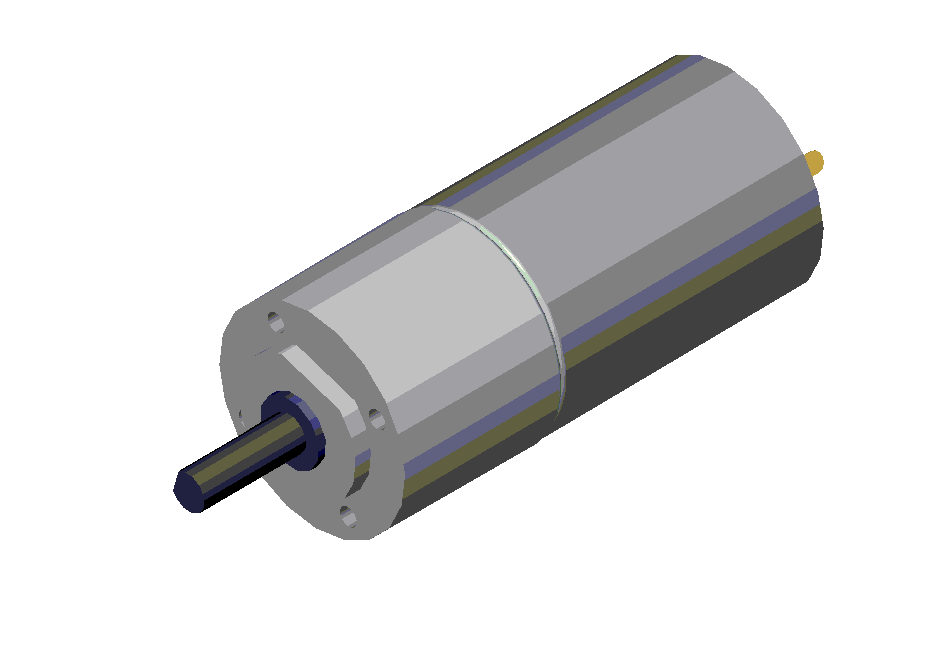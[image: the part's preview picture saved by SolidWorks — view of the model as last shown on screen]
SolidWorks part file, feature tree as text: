
SOLIDWORKS PART (.sldprt)
format: sldprt  version: not decoded by parser v0  size: 169,472 bytes
history: native  units: mm
features: sketch x9, extrude x7, fillet x5, cut_extrude x2, pattern_circular x1 (+8 scaffold rows collapsed)
feature tree (32):
  scaffold x8  (default folders/planes/origin — collapsed)
  sketch  "Sketch1"  dims[D1=21.9mm]
  extrude  "Base-Extrude"  Depth=18mm
  sketch  "Sketch3"  dims[D1=13.88mm D2=5.94mm D3=11.88mm]
  extrude  "Boss-Extrude1"  Depth=1.75mm
  sketch  "Sketch4"  dims[D1=7.01mm]
  extrude  "Boss-Extrude2"  Depth=0.8mm
  sketch  "Sketch5"  dims[D1=3.89mm]
  extrude  "Boss-Extrude3"  Depth=11.5mm
  fillet  "Fillet1"  Radius=0.5mm
  sketch  "Sketch6"  dims[D1=21.66mm]
  extrude  "Boss-Extrude4"  Depth=29.5mm
  fillet  "Fillet2"  Radius=0.5mm
  sketch  "Sketch7"  dims[D1=7.37mm]
  extrude  "Boss-Extrude5"  Depth=2.47mm
  sketch  "Sketch8"  dims[c1.D1=~8.417389mm c2.D1=45.0deg c2.D2=1.93mm c2.D3=0.965mm c2.D4=0.11mm c2.D5=8.5mm c3.D1=8.5mm c3.D3=0.965mm c3.D5=~5.250268mm c3.D6=0.11mm c3.D7=8.5mm c3.D8=1.93mm]
  extrude  "Boss-Extrude6"  Depth=3.18mm
  fillet  "Fillet3"  Radius=0.9mm
  fillet  "Fillet4"  Radius=0.9mm
  fillet  "Fillet5"  Radius=0.9mm
  sketch  "Sketch9"  dims[D1=1.5mm D2=2.0mm D3=4.0mm D4=2.0mm]
  cut_extrude  "Cut-Extrude1"  Depth=8mm
  sketch  "Sketch10"  dims[c1.D2=2.0mm c1.D3=17.5mm c1.D1=~14.25192mm c2.D1=45.0deg c3.D1=8.75mm c3.D3=~6.187184mm]
  cut_extrude  "Cut-Extrude2"  Depth=4mm
  pattern_circular  "CirPattern1"  Count=4 Angle=90deg
decode coverage: 24 of 24 modeling features carry decoded parameters
note: ~ marks probable driven/reference dimensions
note: suppression state not decoded; provenance and decode notes live in map.json
